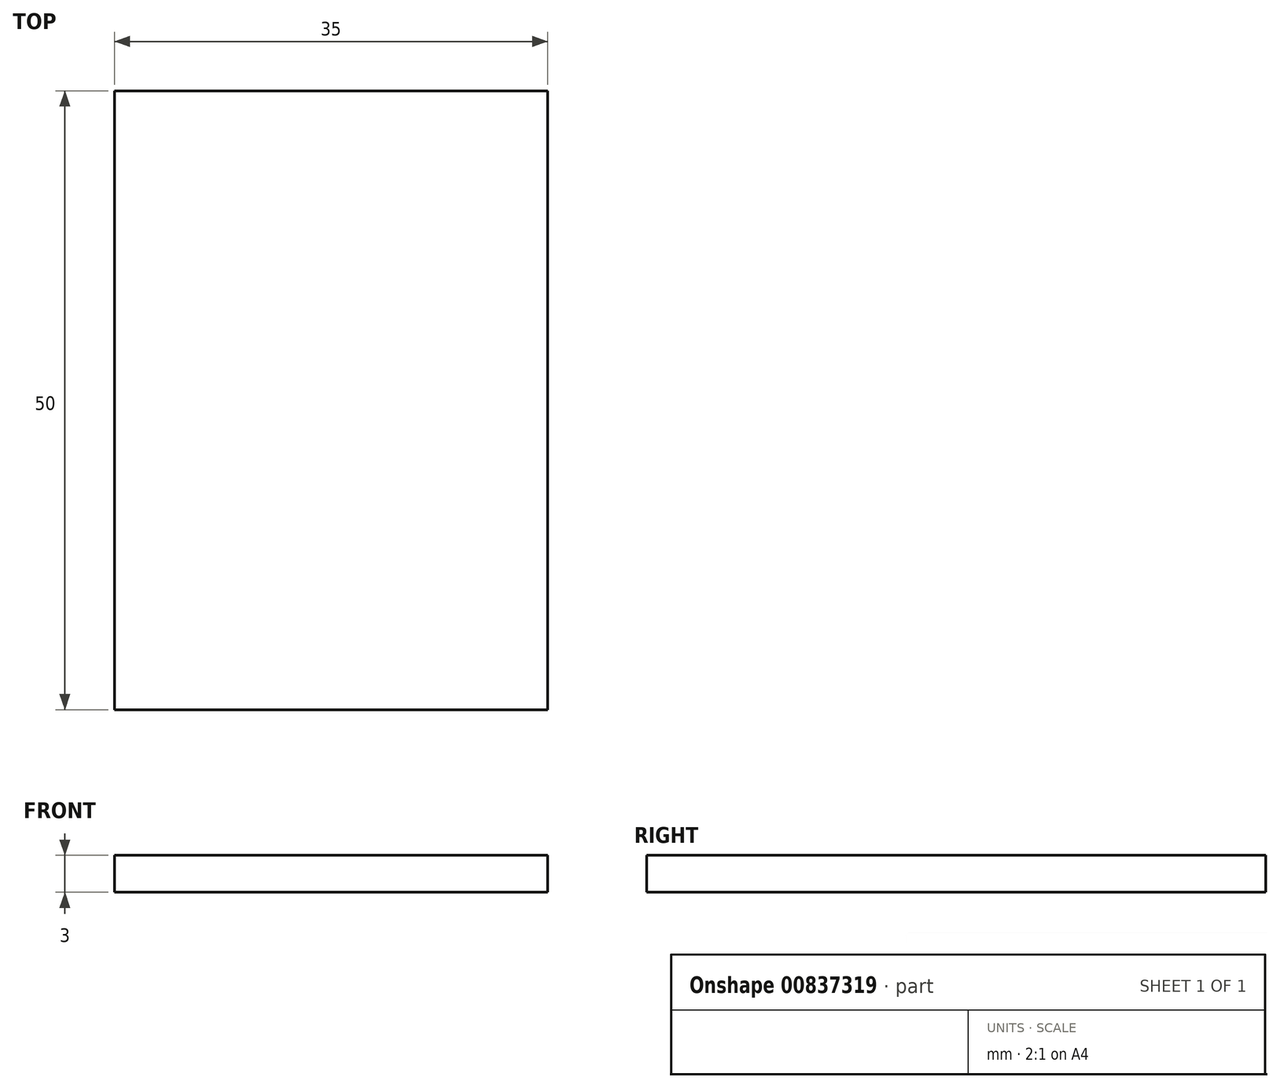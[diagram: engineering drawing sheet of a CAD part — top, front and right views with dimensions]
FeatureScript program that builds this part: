
annotation { "Feature Type Name" : "Feature", "Feature Type Description" : "" }
export const myFeature = defineFeature(function(context is Context, id is Id, definition is map)
    precondition{}
    {
        {
            var Q0;
            Q0=qCreatedBy(makeId("Top.planeOp"),FACE);
            var sketch = newSketch(context, id + "F0", { "sketchPlane" : qUnion([Q0])});
            skLineSegment(sketch, "E0.bottom", {"start": v(0, 0) * mm, "end": v(35, 0) * mm});
            skLineSegment(sketch, "E0.top", {"start": v(0, 50) * mm, "end": v(35, 50) * mm});
            skLineSegment(sketch, "E0.left", {"start": v(0, 0) * mm, "end": v(0, 50) * mm});
            skLineSegment(sketch, "E0.right", {"start": v(35, 0) * mm, "end": v(35, 50) * mm});
            skSolve(sketch);
        }
        {
            var Q0;
            Q0=makeQuery(id+"F0.imprint","IMPRINT",FACE,{"disambiguationData":[TD([[makeQuery(id+"F0.imprint","IMPRINT",EDGE,{"derivedFrom":sQuery(id+"F0.wireOp",EDGE,"E0.bottom")}),1.0]])]});
            extrude(context, id + "F1", {"entities" : qUnion([Q0]), "depth" : 3 * mm, "offsetDistance" : 25 * mm});
        }
    });
